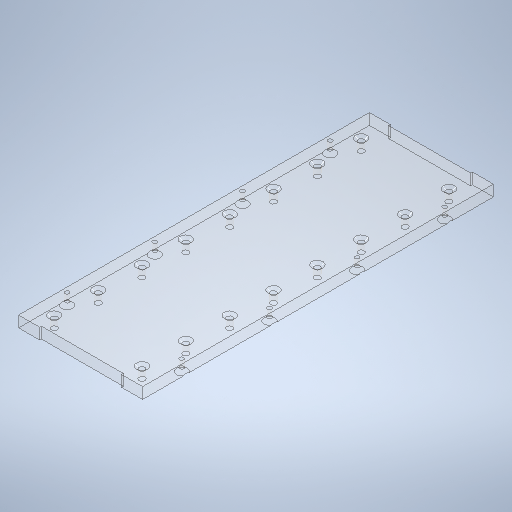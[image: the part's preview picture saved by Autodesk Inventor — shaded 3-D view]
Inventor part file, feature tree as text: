
AUTODESK INVENTOR PART (.ipt)
format: ipt  version: 2025 (Build 290162000, 162)  size: 351,744 bytes
history: native  units: in
note: dims shown in document units (in); Inventor stores cm internally (conversion verified against a paired STEP export)
features: sketch x6, extrude x3, hole x2
ambient origin geometry x8: Origin, YZ Plane, XZ Plane, XY Plane, X Axis, Y Axis, Z Axis, Center Point
bodies: Solid1 (feature_tree)
feature tree (11):
  extrude  "Extrusion1"  Depth=2.7835in
  hole  "Hole1"  [1 undecoded]
  extrude  "Extrusion3"  Depth=0.3937in
  extrude  "Extrusion4"  Depth=0.4724in
  hole  "Hole3"  [1 undecoded]
  sketch  "Sketch1"  dims[d0=7.874in d1=2.7835in]
  sketch  "Sketch2"  dims[d5=0.9843in d6=0.3937in]
  sketch  "Sketch Rectangular Pattern1"  dims[d2=0.25in d3=0.0in d4=1.9685in]
  sketch  "Sketch5"  dims[d7=3.1496in d9=0.9843in d10=0.3937in d12=0.3937in]
  sketch  "Sketch6"  dims[d14=0.1339in d15=0.2362in d16=0.248in d17=0.0787in d18=90.0deg d19=0.315in d20=0.8108in d37=0.4724in]
  sketch  "Sketch7"  dims[d38=0.4724in d39=0.0394in d40=0.0in d41=0.4724in d42=0.4724in d43=0.0394in d44=0.0in d45=0.9843in d46=0.1053in d47=0.9843in d48=1.9685in d49=1.9685in d50=0.1053in d51=0.0945in d52=0.2362in d53=0.248in d54=0.1181in d55=90.0deg d56=0.3937in d57=0.8108in]
note: 2 required parameter values undecoded (feature->parameter linkage not recoverable at this tier; creation-order binding heuristic only, values carry confidence <= 0.55)
